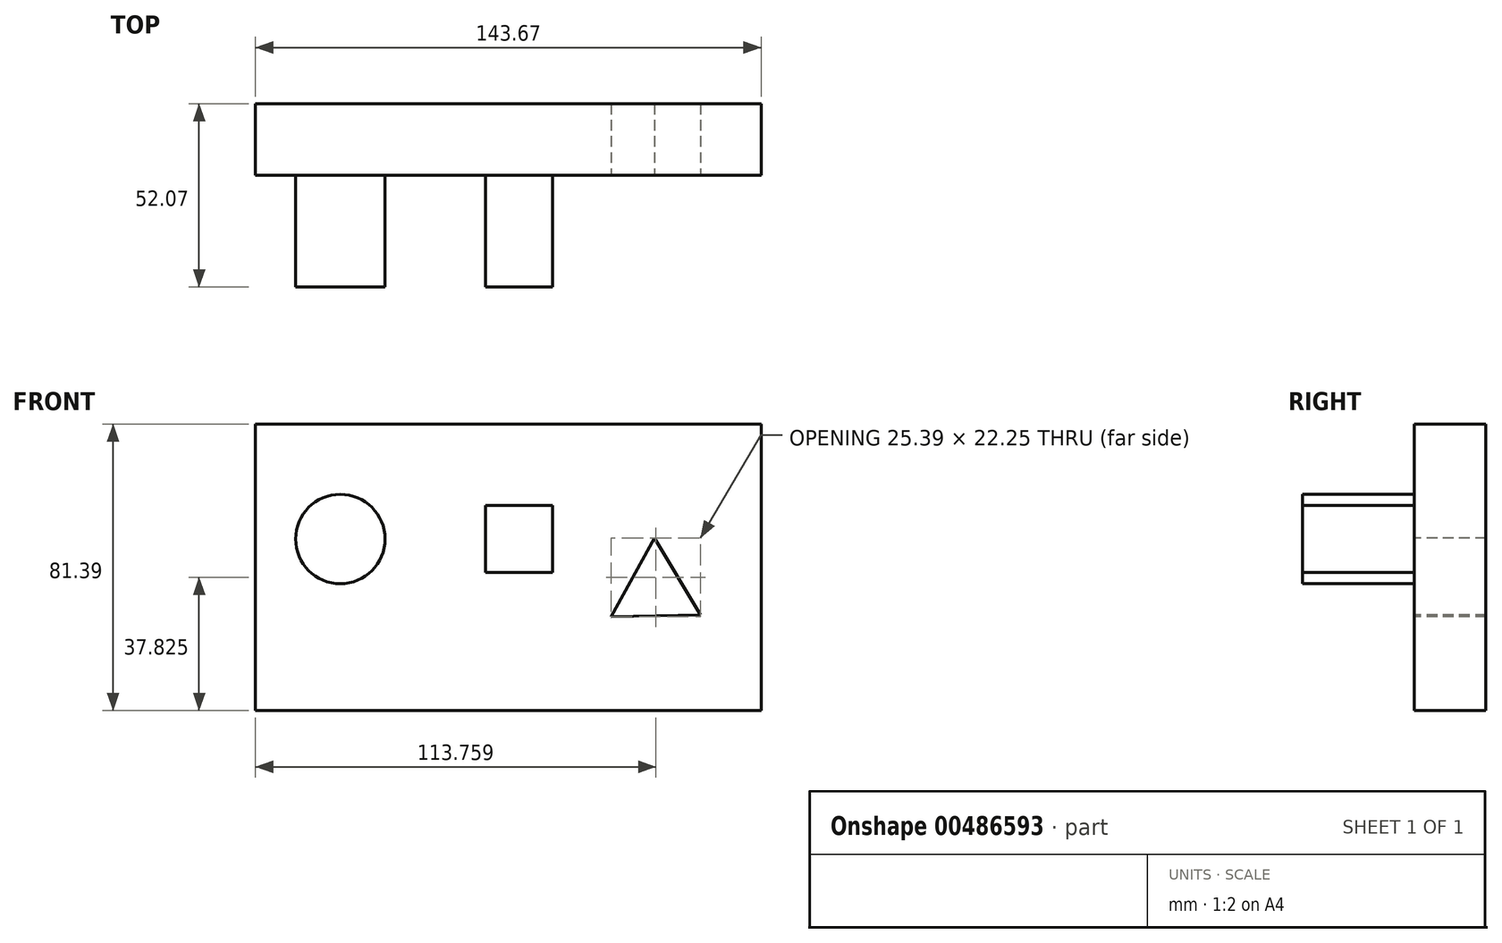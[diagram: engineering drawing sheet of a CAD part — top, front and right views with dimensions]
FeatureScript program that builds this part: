
annotation { "Feature Type Name" : "Feature", "Feature Type Description" : "" }
export const myFeature = defineFeature(function(context is Context, id is Id, definition is map)
    precondition{}
    {
        {
            var Q0;
            Q0=qCreatedBy(makeId("Front.planeOp"),FACE);
            var sketch = newSketch(context, id + "F0", { "sketchPlane" : qUnion([Q0])});
            skLineSegment(sketch, "E0", {"start": v(1.36, -11.47) * mm, "end": v(6.97, -14.44) * mm});
            skCircle(sketch, "E1.cCircle", {"center": v(6.97, -14.44) * mm, "radius": 7.33 * mm, "construction": true});
            skLineSegment(sketch, "E1.0", {"start": v(6.67, 0.22) * mm, "end": v(19.82, -21.52) * mm});
            skLineSegment(sketch, "E1.1", {"start": v(19.82, -21.52) * mm, "end": v(-5.58, -22.03) * mm});
            skLineSegment(sketch, "E1.2", {"start": v(-5.58, -22.03) * mm, "end": v(6.67, 0.22) * mm});
            skPoint(sketch, "E1.0.midPoint", {"position": v(13.24, -10.65) * mm});
            skLineSegment(sketch, "E2", {"start": v(0, 0) * mm, "end": v(-31.75, 0) * mm});
            skLineSegment(sketch, "E3.bottom", {"start": v(-41.27, 9.53) * mm, "end": v(-22.22, 9.53) * mm});
            skLineSegment(sketch, "E3.top", {"start": v(-41.28, -9.52) * mm, "end": v(-22.22, -9.52) * mm});
            skLineSegment(sketch, "E3.left", {"start": v(-41.27, 9.53) * mm, "end": v(-41.28, -9.53) * mm});
            skLineSegment(sketch, "E3.right", {"start": v(-22.22, 9.53) * mm, "end": v(-22.22, -9.53) * mm});
            skPoint(sketch, "E3.middle", {"position": v(-31.75, 0) * mm});
            skLineSegment(sketch, "E4", {"start": v(-31.75, 0) * mm, "end": v(-82.55, 0) * mm});
            skCircle(sketch, "E5", {"center": v(-82.55, 0) * mm, "radius": 12.7 * mm});
            skLineSegment(sketch, "E6.bottom", {"start": v(-106.64, 32.66) * mm, "end": v(37.03, 32.66) * mm});
            skLineSegment(sketch, "E6.top", {"start": v(-106.64, -48.73) * mm, "end": v(37.03, -48.73) * mm});
            skLineSegment(sketch, "E6.left", {"start": v(-106.64, 32.66) * mm, "end": v(-106.64, -48.73) * mm});
            skLineSegment(sketch, "E6.right", {"start": v(37.03, 32.66) * mm, "end": v(37.03, -48.73) * mm});
            skSolve(sketch);
        }
        {
            var Q0;
            Q0=makeQuery(id+"F0.imprint","IMPRINT",FACE,{"disambiguationData":[TD([[makeQuery(id+"F0.imprint","IMPRINT",EDGE,{"derivedFrom":sQuery(id+"F0.wireOp",EDGE,"E5")}),1.0]])]});
            var Q1;
            {var subQ1=sQuery(id+"F0.wireOp",EDGE,"E3.bottom");Q1=makeQuery(id+"F0.imprint","IMPRINT",FACE,{"disambiguationData":[TD([[makeQuery(id+"F0.imprint","IMPRINT",EDGE,{"derivedFrom":subQ1}),-1.0]])]});}
            var Q2;
            {var subQ1=sQuery(id+"F0.wireOp",EDGE,"E3.top");Q2=makeQuery(id+"F0.imprint","IMPRINT",FACE,{"disambiguationData":[TD([[makeQuery(id+"F0.imprint","IMPRINT",EDGE,{"derivedFrom":subQ1}),1.0]])]});}
            extrude(context, id + "F1", {"entities" : qUnion([Q0, Q1, Q2]), "depth" : 31.75 * mm});
        }
        {
            var Q0;
            Q0 = qSketchRegion(id + "F0", true);
            var Q1;
            Q1=makeQuery(id+"FLBcnQlaQkKcYMF_2.opExtrude","CAP_FACE",FACE,{"disambiguationData":[OSD([sQuery(id+"F0.wireOp",EDGE,"E1.0"),sQuery(id+"F0.wireOp",EDGE,"E1.1"),sQuery(id+"F0.wireOp",EDGE,"E1.2")])],"isStart":false});
            var Q2;
            Q2=makeQuery(id+"F0.imprint","IMPRINT",FACE,{"disambiguationData":[TD([[makeQuery(id+"F0.imprint","IMPRINT",EDGE,{"derivedFrom":sQuery(id+"F0.wireOp",EDGE,"E5")}),1.0]])]});
            var Q3;
            {var subQ1=sQuery(id+"F0.wireOp",EDGE,"E3.top");Q3=makeQuery(id+"F0.imprint","IMPRINT",FACE,{"disambiguationData":[TD([[makeQuery(id+"F0.imprint","IMPRINT",EDGE,{"derivedFrom":subQ1}),1.0]])]});}
            var Q4;
            {var subQ1=sQuery(id+"F0.wireOp",EDGE,"E3.bottom");Q4=makeQuery(id+"F0.imprint","IMPRINT",FACE,{"disambiguationData":[TD([[makeQuery(id+"F0.imprint","IMPRINT",EDGE,{"derivedFrom":subQ1}),-1.0]])]});}
            extrude(context, id + "F2", {"entities" : qUnion([Q0, Q1, Q2, Q3, Q4]), "oppositeDirection" : true, "depth" : 20.32 * mm});
        }
    });
